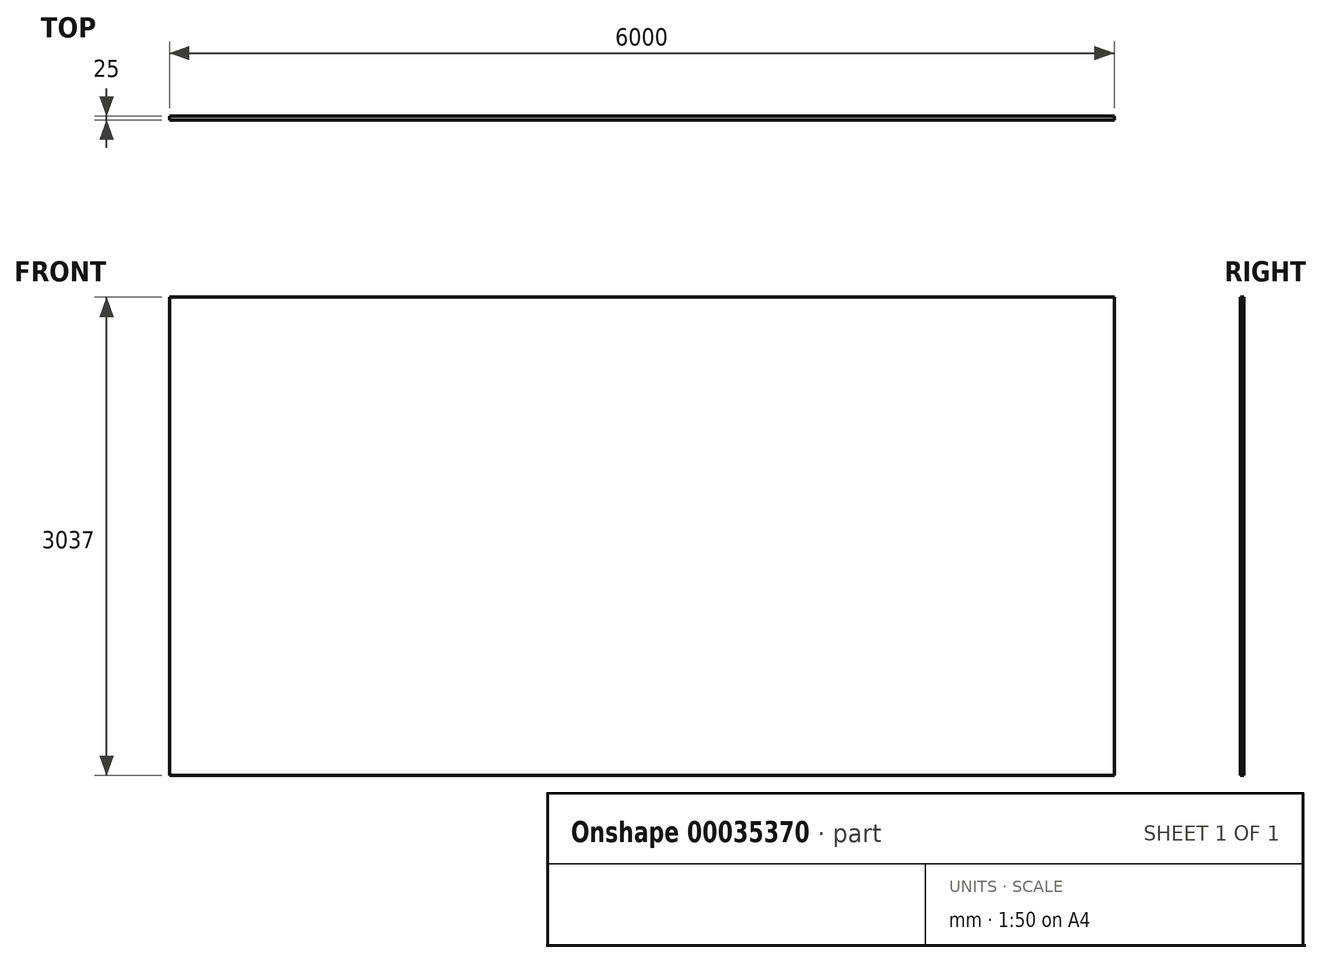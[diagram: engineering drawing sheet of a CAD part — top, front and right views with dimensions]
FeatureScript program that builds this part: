
annotation { "Feature Type Name" : "Feature", "Feature Type Description" : "" }
export const myFeature = defineFeature(function(context is Context, id is Id, definition is map)
    precondition{}
    {
        {
            var Q0;
            Q0=qCreatedBy(makeId("Front.planeOp"),FACE);
            var sketch = newSketch(context, id + "F0", { "sketchPlane" : qUnion([Q0])});
            skLineSegment(sketch, "E0.rect.bottom", {"start": v(3000, -1518.5) * mm, "end": v(-3000, -1518.5) * mm});
            skLineSegment(sketch, "E0.rect.top", {"start": v(3000, 1518.5) * mm, "end": v(-3000, 1518.5) * mm});
            skLineSegment(sketch, "E0.rect.left", {"start": v(3000, -1518.5) * mm, "end": v(3000, 1518.5) * mm});
            skLineSegment(sketch, "E0.rect.right", {"start": v(-3000, -1518.5) * mm, "end": v(-3000, 1518.5) * mm});
            skPoint(sketch, "E0.rect.middle", {"position": v(0, 0) * mm});
            skSolve(sketch);
        }
        {
            var Q0;
            Q0=makeQuery(id+"F0.imprint","IMPRINT",FACE,{"disambiguationData":[TD([[makeQuery(id+"F0.imprint","IMPRINT",EDGE,{"derivedFrom":sQuery(id+"F0.wireOp",EDGE,"E0.rect.bottom")}),-1.0]])]});
            extrude(context, id + "F1", {"entities" : qUnion([Q0]), "depth" : 25 * mm});
        }
    });
